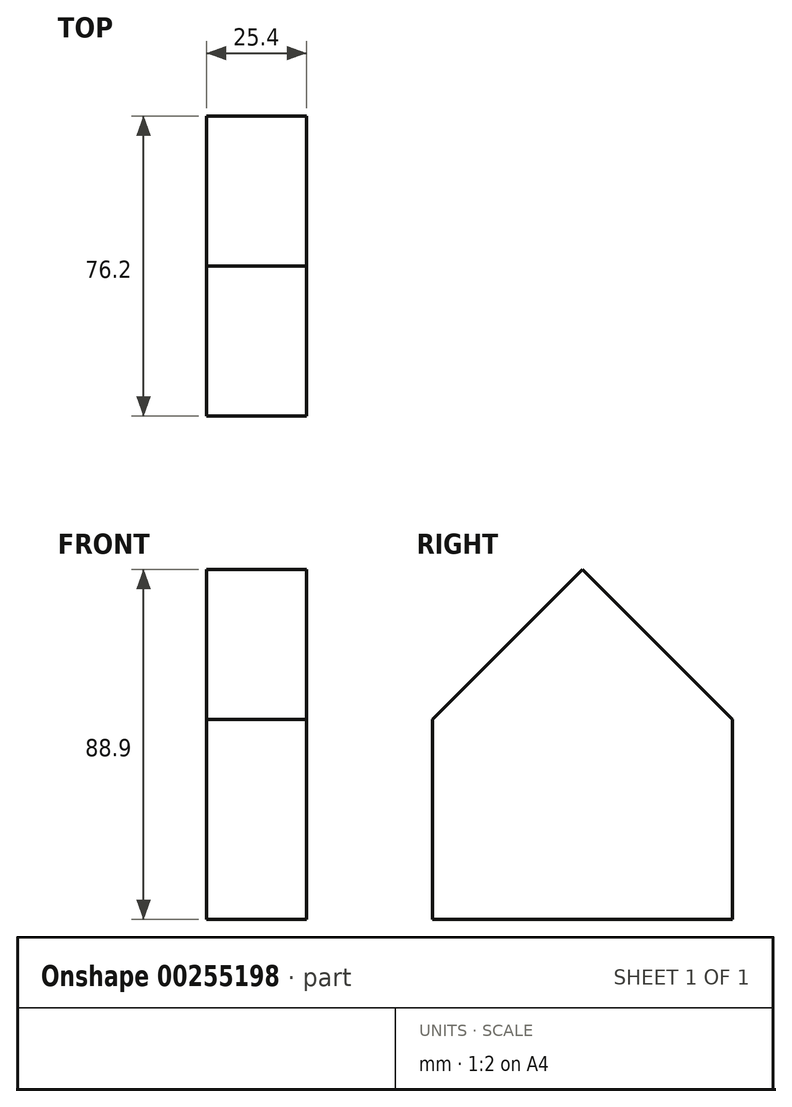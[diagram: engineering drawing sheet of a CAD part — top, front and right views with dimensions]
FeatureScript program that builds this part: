
annotation { "Feature Type Name" : "Feature", "Feature Type Description" : "" }
export const myFeature = defineFeature(function(context is Context, id is Id, definition is map)
    precondition{}
    {
        {
            var Q0;
            Q0=qCreatedBy(makeId("Right.planeOp"),FACE);
            var sketch = newSketch(context, id + "F0", { "sketchPlane" : qUnion([Q0])});
            skLineSegment(sketch, "E0.top", {"start": v(76.2, 0) * mm, "end": v(0, 0) * mm});
            skLineSegment(sketch, "E0.left", {"start": v(76.2, 50.8) * mm, "end": v(76.2, 0) * mm});
            skLineSegment(sketch, "E0.right", {"start": v(0, 50.8) * mm, "end": v(0, 0) * mm});
            skLineSegment(sketch, "E1", {"start": v(0, 50.8) * mm, "end": v(38.1, 88.9) * mm});
            skLineSegment(sketch, "E2", {"start": v(38.1, 88.9) * mm, "end": v(76.2, 50.8) * mm});
            skSolve(sketch);
        }
        {
            var Q0;
            Q0=makeQuery(id+"F0.imprint","IMPRINT",FACE,{"disambiguationData":[TD([[makeQuery(id+"F0.imprint","IMPRINT",EDGE,{"derivedFrom":sQuery(id+"F0.wireOp",EDGE,"E0.top")}),-1.0]])]});
            extrude(context, id + "F1", {"entities" : qUnion([Q0]), "depth" : 25.4 * mm});
        }
    });
